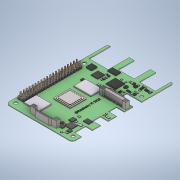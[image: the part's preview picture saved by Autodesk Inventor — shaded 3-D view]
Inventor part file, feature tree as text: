
AUTODESK INVENTOR PART (.ipt)
format: ipt  version: 2020 (Build 240168000, 168)  size: 3,276,288 bytes
history: native  units: in
note: dims shown in document units (in); Inventor stores cm internally (conversion verified against a paired STEP export)
features: extrude x18, sketch x5, fillet x1, chamfer x1
ambient origin geometry x8: Origin, YZ Plane, XZ Plane, XY Plane, X Axis, Y Axis, Z Axis, Center Point
bodies: Solid1 (feature_tree)
feature tree (25):
  sketch  "Sketch1"  dims[d24=0.1969in d25=0.1969in]
  extrude  "Extrusion1"  Depth=0.1969in
  extrude  "Extrusion2"  Depth=0.1181in
  extrude  "Extrusion3"  Depth=0.0591in
  extrude  "Extrusion4"  Depth=0.0394in
  extrude  "Extrusion5"  Depth=0.0394in
  extrude  "Extrusion6"  Depth=0.0394in
  extrude  "Extrusion7"  Depth=0.0394in
  extrude  "Extrusion8"  Depth=0.0394in
  extrude  "Extrusion9"  Depth=0.0394in
  extrude  "Extrusion10"  Depth=0.0394in
  extrude  "Extrusion11"  Depth=0.0394in
  extrude  "Extrusion13"  Depth=0.0394in
  sketch  "Sketch2"  dims[d31=0.1181in d32=0.1181in]
  extrude  "Extrusion14"  Depth=0.0394in
  extrude  "Extrusion15"  Depth=0.0394in
  extrude  "Extrusion16"  Depth=0.0394in
  sketch  "Sketch6"  dims[d33=0.0591in d34=0.0591in]
  extrude  "Extrusion19"  Depth=0.0394in
  extrude  "Extrusion20"  Depth=0.0394in
  sketch  "Sketch7"  dims[d37=0.0394in d38=0.0394in]
  fillet  "Fillet1"  Radius=0.0787in
  chamfer  "Chamfer1"  Distance=0.0787in
  extrude  "Extrusion21"  Depth=0.0787in
  sketch  "Sketch8"  dims[d39=0.0394in d40=0.0394in d41=0.0394in d42=0.0394in d43=0.0394in d44=0.0394in d48=0.0394in d49=0.0394in d50=0.0394in d51=0.0394in d52=0.0394in d53=0.0394in d54=0.0394in d55=0.0394in d58=0.0787in d59=0.0787in d60=0.0787in d61=0.0787in d62=0.0787in d63=0.0787in d64=0.0787in d65=0.0787in d68=0.0394in d69=0.0394in d70=0.0394in d71=0.0394in d72=0.0394in d73=0.0394in d74=0.0394in d75=0.0394in d76=0.0394in d77=0.0394in d78=0.0394in d79=0.0394in d80=0.0394in d81=0.0394in d82=0.0394in d83=0.0394in d84=0.0394in d85=0.0394in d86=0.0394in d87=0.0394in d88=0.0394in d89=0.0394in d90=0.0394in d91=0.0394in d92=0.0394in d93=0.0394in d94=0.0394in d95=0.0394in d96=0.0394in d97=0.0394in d98=0.0394in d99=0.0394in d100=0.0394in d101=0.0394in d102=0.0394in d103=0.0394in d104=0.0394in d105=0.0394in d106=0.0394in d107=0.0394in d108=0.0394in d109=0.0394in d110=0.0394in d112=0.0394in d113=0.0394in d114=0.0394in d115=0.0394in d116=0.0394in d117=0.0394in d118=0.0394in d119=0.0394in d120=0.0394in d121=0.0394in d122=0.0394in d123=0.0394in d124=0.0394in d125=0.0394in d126=0.0394in d127=0.0394in d128=0.0394in d129=0.0394in d130=0.0394in d131=0.0394in d132=0.0394in d133=0.0394in d134=0.0394in d135=0.0394in d136=0.0394in d137=0.0394in d138=0.0394in d139=0.0394in d140=0.0394in d141=0.0394in d142=0.0394in d143=0.0394in d144=0.0394in d145=0.0394in d146=0.0394in d147=0.0394in d148=0.0394in d149=0.0394in d150=0.0394in d151=0.0394in d152=0.0394in d153=0.0394in d154=0.0394in d155=0.0394in d156=0.0394in d157=0.0394in d158=0.0394in d159=0.0394in d162=0.0394in d163=0.0394in d164=0.0394in d165=0.0394in d166=0.0394in d167=0.0394in d168=0.0394in d169=0.0394in d170=0.0394in d171=0.0394in d172=0.0394in d173=0.0394in d174=0.0394in d175=0.0394in d176=0.0394in d177=0.0394in d178=0.0394in d179=0.0394in d180=0.0394in d181=0.0394in d182=0.0394in d183=0.0394in d184=0.0394in d185=0.0394in d186=0.0394in d187=0.0394in d188=0.0394in d189=0.0394in d190=0.0394in d191=0.0394in d192=0.0394in d193=0.0394in d194=0.0394in d195=0.0394in d198=0.0394in d199=0.0394in d200=0.0394in d201=0.0394in d202=0.0394in d203=0.0394in d204=0.0394in d205=0.0394in d206=0.0394in d207=0.0394in d208=0.0394in d209=0.0394in d210=0.0394in d211=0.0394in d212=0.0394in d213=0.0394in d214=0.0394in d215=0.0394in d216=0.0394in d217=0.0394in d218=0.0394in d219=0.0394in d220=0.0394in d221=0.0394in d222=0.0394in d223=0.0394in d224=0.0394in d225=0.0394in d226=0.0394in d227=0.0394in d228=0.0394in d229=0.0394in d230=0.0394in d231=0.0394in d247=0.0394in d248=0.0in d250=0.0591in d251=0.0in d252=0.0787in d253=0.0in d254=0.0984in d255=0.0in d256=0.1181in d257=0.0in d258=0.0984in d259=0.0in d260=0.0787in d261=0.0in d262=0.1575in d263=0.0in d264=0.3937in d265=0.0in d266=0.3937in d267=0.0in d268=0.1575in d269=0.0in d272=0.4134in d273=0.0in d274=0.0787in d275=0.0in d276=0.0591in d277=0.0in d278=0.0394in d279=0.0in d286=0.0394in d287=0.0in d288=0.0394in d289=0.0in d290=0.0079in d291=0.0787in d292=0.0787in d293=45.0deg d295=0.0118in d296=0.0in d249=0.0197in]
